# Revit family: Albardilla MA remate.C-1
name_source: partatom
category: Modelos genéricos
units: mm (PartAtom-declared; Revit-internal decimal feet)

## family parameters
Compartido = No
Corte con vacíos al cargar = No
Cota de conector redondo = Diámetro de uso
Puede alojar armadura = No
Punto de cálculo de habitación = No
Se basa en plano de trabajo = No
Siempre vertical = No
Tipo de pieza = Normal

## types (5) — shared parameters
Altura = 44 mm  [stored 0.144357 ft]
Descripción = Pieza de hormigón polímero con anclaje de acero inoxidable.
Fabricante = ULMA Architectural Solutions
Longitud vaciado = 735 mm
Material = Hormigón polímero STONEO. Color C-1
URL = https://www.ulmaarchitectural.com
zero-valued in all types: Elevación por defecto

## per-type parameters (varying)
| type | Ancho | Ancho doble | Ancho total | Ancho vaciado | Mitad | Modelo |
| A12T | 120 mm  [stored 0.393701 ft] | 30 mm  [stored 0.0984252 ft] | 170 mm  [stored 0.557743 ft] | 138 mm  [stored 0.452756 ft] | 85 mm  [stored 0.278871 ft] | Albardilla MA12 remate |
| A14T | 140 mm  [stored 0.459318 ft] | 35 mm  [stored 0.114829 ft] | 190 mm | 158 mm | 95 mm | Albardilla MA14 remate |
| A17T | 170 mm  [stored 0.557743 ft] | 43 mm | 220 mm  [stored 0.721785 ft] | 188 mm  [stored 0.616798 ft] | 110 mm  [stored 0.360892 ft] | Albardilla MA17 remate |
| A22T | 220 mm  [stored 0.721785 ft] | 55 mm  [stored 0.180446 ft] | 270 mm  [stored 0.885827 ft] | 238 mm  [stored 0.78084 ft] | 135 mm  [stored 0.442913 ft] | Albardilla MA22 remate |
| A19T | 190 mm | 48 mm | 240 mm  [stored 0.787402 ft] | 208 mm  [stored 0.682415 ft] | 120 mm  [stored 0.393701 ft] | Albardilla MA19 remate |

note: column(s) folded — value = type name in every type: Código de montaje

note: [stored X ft] marks values corroborated as IEEE doubles in the binary element streams (Revit-internal decimal feet)
